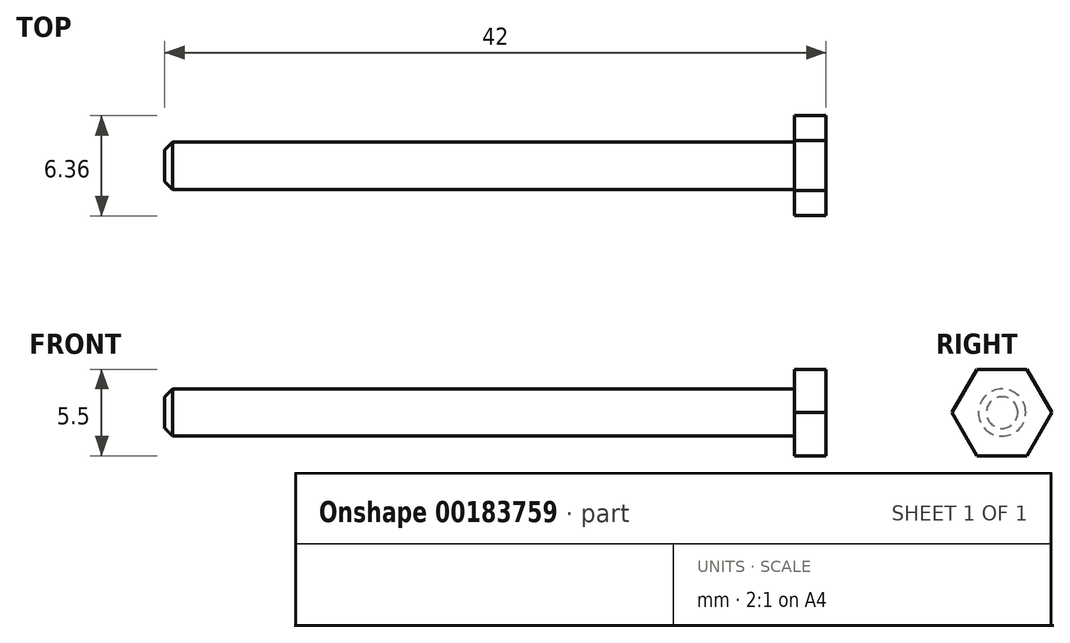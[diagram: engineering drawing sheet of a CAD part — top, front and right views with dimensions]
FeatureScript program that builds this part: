
annotation { "Feature Type Name" : "Feature", "Feature Type Description" : "" }
export const myFeature = defineFeature(function(context is Context, id is Id, definition is map)
    precondition{}
    {
        {
            var Q0;
            Q0=qCreatedBy(makeId("Right.planeOp"),FACE);
            var sketch = newSketch(context, id + "F0", { "sketchPlane" : qUnion([Q0])});
            skCircle(sketch, "E0.cCircle", {"center": v(0, 0) * mm, "radius": 2.75 * mm, "construction": true});
            skLineSegment(sketch, "E0.0", {"start": v(-1.59, 2.75) * mm, "end": v(1.59, 2.75) * mm});
            skLineSegment(sketch, "E0.1", {"start": v(1.59, 2.75) * mm, "end": v(3.18, 0) * mm});
            skLineSegment(sketch, "E0.2", {"start": v(3.18, 0) * mm, "end": v(1.59, -2.75) * mm});
            skLineSegment(sketch, "E0.3", {"start": v(1.59, -2.75) * mm, "end": v(-1.59, -2.75) * mm});
            skLineSegment(sketch, "E0.4", {"start": v(-1.59, -2.75) * mm, "end": v(-3.18, 0) * mm});
            skLineSegment(sketch, "E0.5", {"start": v(-3.18, 0) * mm, "end": v(-1.59, 2.75) * mm});
            skPoint(sketch, "E0.0.midPoint", {"position": v(0, 2.75) * mm});
            skSolve(sketch);
        }
        {
            var Q0;
            Q0=makeQuery(id+"F0.imprint","IMPRINT",FACE,{"disambiguationData":[TD([[makeQuery(id+"F0.imprint","IMPRINT",EDGE,{"derivedFrom":sQuery(id+"F0.wireOp",EDGE,"E0.0")}),-1.0]])]});
            extrude(context, id + "F1", {"entities" : qUnion([Q0]), "depth" : 2 * mm});
        }
        {
            var Q0;
            Q0=qCreatedBy(makeId("Right.planeOp"),FACE);
            var sketch = newSketch(context, id + "F2", { "sketchPlane" : qUnion([Q0])});
            skCircle(sketch, "E1", {"center": v(0, 0) * mm, "radius": 1.5 * mm});
            skSolve(sketch);
        }
        {
            var Q0;
            Q0=makeQuery(id+"F2.imprint","IMPRINT",FACE,{"disambiguationData":[TD([[makeQuery(id+"F2.imprint","IMPRINT",EDGE,{"derivedFrom":sQuery(id+"F2.wireOp",EDGE,"E1")}),1.0]])]});
            extrude(context, id + "F3", {"entities" : qUnion([Q0]), "operationType" : NewBodyOperationType.ADD, "oppositeDirection" : true, "depth" : 40 * mm});
        }
        {
            var Q0;
            Q0=makeQuery(id+"F3.opExtrude","CAP_EDGE",EDGE,{"disambiguationData":[OSD([sQuery(id+"F2.wireOp",EDGE,"E1")])],"isStart":false});
            chamfer(context, id + "F4", {"entities" : qUnion([Q0]), "width" : .5 * mm, "tangentPropagation" : true});
        }
    });
